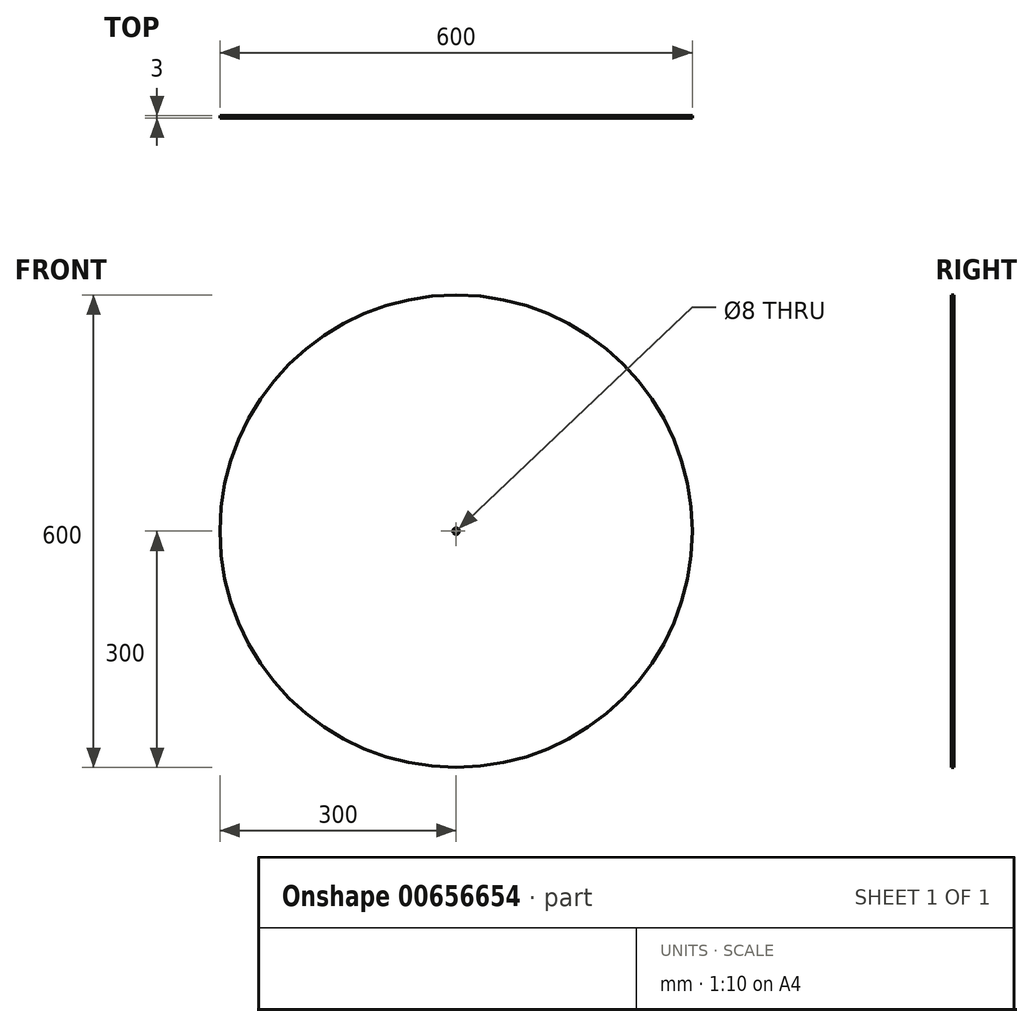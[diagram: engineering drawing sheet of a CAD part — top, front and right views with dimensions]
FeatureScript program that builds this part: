
annotation { "Feature Type Name" : "Feature", "Feature Type Description" : "" }
export const myFeature = defineFeature(function(context is Context, id is Id, definition is map)
    precondition{}
    {
        {
            var Q0;
            Q0=qCreatedBy(makeId("Front.planeOp"),FACE);
            var sketch = newSketch(context, id + "F0", { "sketchPlane" : qUnion([Q0])});
            skCircle(sketch, "E0", {"center": v(0, 0) * mm, "radius": 300 * mm});
            skCircle(sketch, "E1", {"center": v(0, 0) * mm, "radius": 4 * mm});
            skSolve(sketch);
        }
        {
            var Q0;
            Q0 = qSketchRegion(id + "F0", true);
            extrude(context, id + "F1", {"entities" : qUnion([Q0]), "depth" : 3 * mm, "offsetDistance" : 25 * mm});
        }
    });
